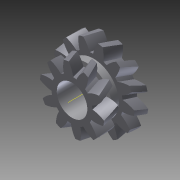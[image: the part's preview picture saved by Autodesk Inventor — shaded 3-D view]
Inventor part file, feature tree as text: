
AUTODESK INVENTOR PART (.ipt)
format: ipt  version: 2012 (Build 160160000, 160)  size: 572,416 bytes
history: native  units: in
note: dims shown in document units (in); Inventor stores cm internally (conversion verified against a paired STEP export)
features: other x5, extrude x3, sketch x3, projected_geometry x1
ambient origin geometry x8: Origin, YZ Plane, XZ Plane, XY Plane, X Axis, Y Axis, Z Axis, Center Point
bodies: Solid2 (feature_tree)
feature tree (12):
  other  "LargeSmallTransferGear.iam"
  other  "BlankGearLargeAndSmall.ipt:1"
  other  "Spur Gear1:1"
  other  "Spur Gear2:1"
  extrude  "Extrusion3"  Depth=0.3937in TaperAngle=0.0deg
  extrude  "Extrusion4"  Depth=0.3346in
  extrude  "Extrusion5"  [1 undecoded]
  other  "Work Axis2"
  sketch  "Sketch4"  dims[d5=0.3937in d6=0.3937in d7=0.0in]
  projected_geometry  "Projected Loop2"
  sketch  "Sketch5"  dims[d8=0.3937in d9=0.0in d10=0.3346in]
  sketch  "Sketch6"  dims[d12=0.3937in d13=0.0in]
note: 1 required parameter value undecoded (feature->parameter linkage not recoverable at this tier; creation-order binding heuristic only, values carry confidence <= 0.55)
